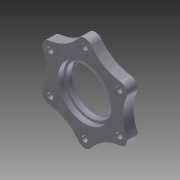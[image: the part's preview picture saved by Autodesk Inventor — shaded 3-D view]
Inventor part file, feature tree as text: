
AUTODESK INVENTOR PART (.ipt)
format: ipt  version: 2012 (Build 160160000, 160)  size: 312,320 bytes
history: native  units: in
note: dims shown in document units (in); Inventor stores cm internally (conversion verified against a paired STEP export)
features: extrude x4, other x3, sketch x2, chamfer x1
ambient origin geometry x8: Origin, YZ Plane, XZ Plane, XY Plane, X Axis, Y Axis, Z Axis, Center Point
bodies: Solid1 (feature_tree)
feature tree (10):
  other  "Shaft Collar.IGS1"
  sketch  "Sketch2"  dims[d0=0.25in d1=0.0in d2=0.125in d3=0.0in]
  extrude  "Extrusion1"  Depth=0.125in TaperAngle=0.0deg
  extrude  "Extrusion2"  Depth=0.125in TaperAngle=0.0deg
  sketch  "Sketch3"  dims[d4=1.25in d5=0.125in d6=0.0in d7=0.125in d8=0.0in d9=0.118in d10=0.125in d11=45.0deg]
  extrude  "Extrusion3"  Depth=0.125in TaperAngle=0.0deg
  extrude  "Extrusion4"  Depth=0.118in TaperAngle=45.0deg
  chamfer  "Chamfer1"  [1 undecoded]
  other  "Composite1"
  other  "Srf1"
note: 1 required parameter value undecoded (feature->parameter linkage not recoverable at this tier; creation-order binding heuristic only, values carry confidence <= 0.55)
